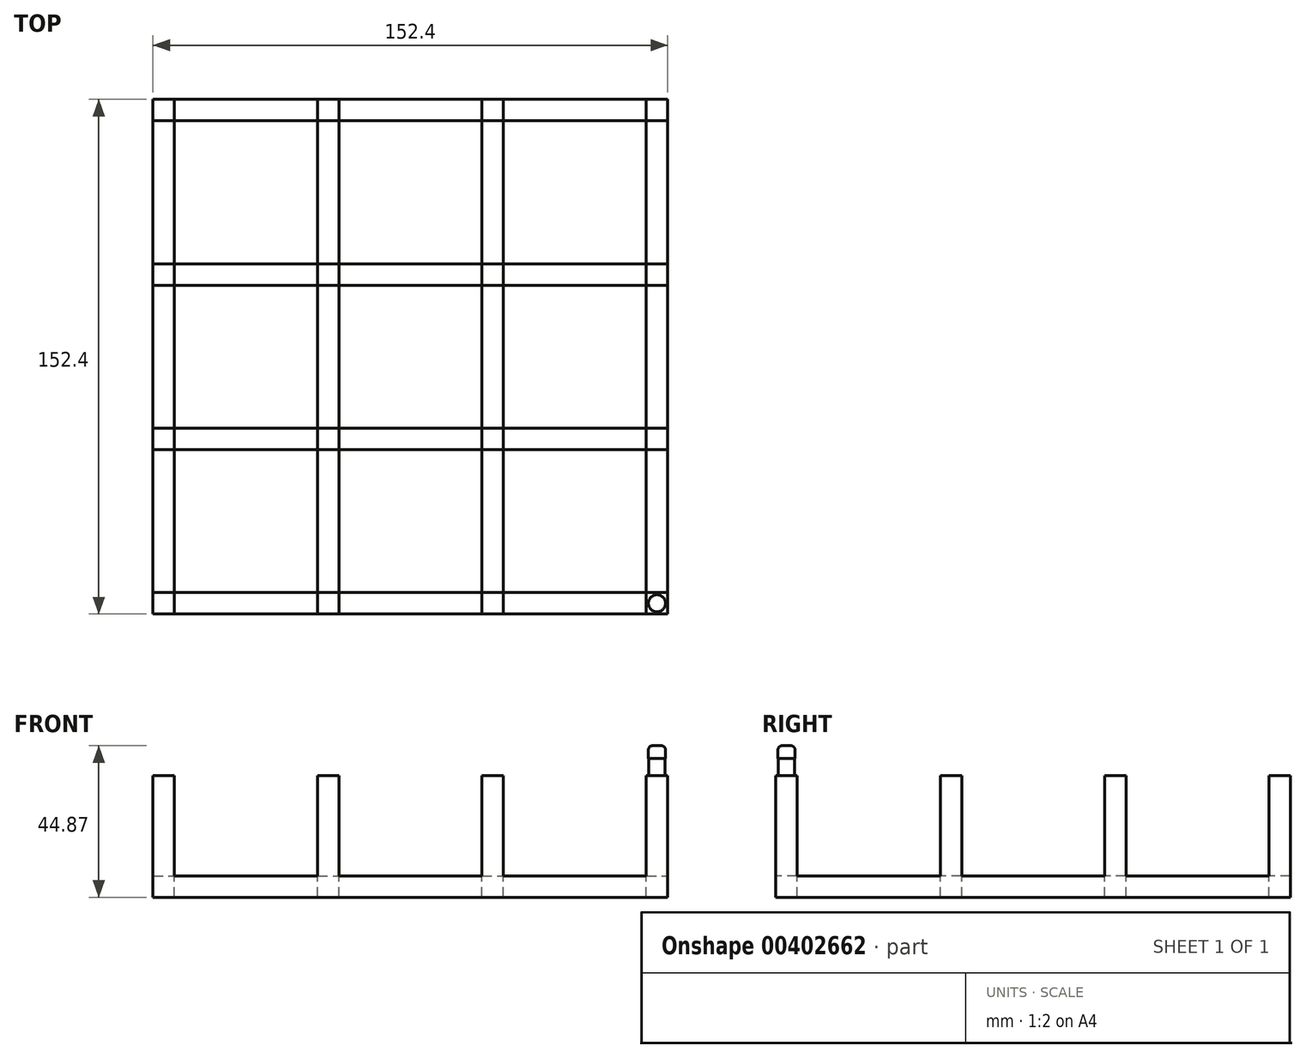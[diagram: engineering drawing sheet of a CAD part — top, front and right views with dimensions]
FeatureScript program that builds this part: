
annotation { "Feature Type Name" : "Feature", "Feature Type Description" : "" }
export const myFeature = defineFeature(function(context is Context, id is Id, definition is map)
    precondition{}
    {
        {
            var Q0;
            Q0=qCreatedBy(makeId("Top.planeOp"),FACE);
            var sketch = newSketch(context, id + "F0", { "sketchPlane" : qUnion([Q0])});
            skLineSegment(sketch, "E0.bottom", {"start": v(0, 0) * mm, "end": v(152.4, 0) * mm});
            skLineSegment(sketch, "E0.top", {"start": v(0, 152.4) * mm, "end": v(152.4, 152.4) * mm});
            skLineSegment(sketch, "E0.left", {"start": v(0, 0) * mm, "end": v(0, 152.4) * mm});
            skLineSegment(sketch, "E0.right", {"start": v(152.4, 0) * mm, "end": v(152.4, 152.4) * mm});
            skSolve(sketch);
        }
        {
            var Q0;
            Q0 = qSketchRegion(id + "F0", true);
            extrude(context, id + "F1", {"entities" : qUnion([Q0]), "depth" : 35.98 * mm});
        }
        {
            var Q0;
            Q0=makeQuery(id+"F1.opExtrude","SWEPT_FACE",FACE,{"disambiguationData":[OSD([sQuery(id+"F0.wireOp",EDGE,"E0.bottom")])]});
            var sketch = newSketch(context, id + "F2", { "sketchPlane" : qUnion([Q0])});
            skLineSegment(sketch, "E1.bottom", {"start": v(6.35, 35.98) * mm, "end": v(48.68, 35.98) * mm});
            skLineSegment(sketch, "E1.top", {"start": v(6.35, 6.35) * mm, "end": v(48.68, 6.35) * mm});
            skLineSegment(sketch, "E1.left", {"start": v(6.35, 35.98) * mm, "end": v(6.35, 6.35) * mm});
            skLineSegment(sketch, "E1.right", {"start": v(48.68, 35.98) * mm, "end": v(48.68, 6.35) * mm});
            skLineSegment(sketch, "E2.bottom", {"start": v(55.03, 35.98) * mm, "end": v(97.37, 35.98) * mm});
            skLineSegment(sketch, "E2.top", {"start": v(55.03, 6.35) * mm, "end": v(97.37, 6.35) * mm});
            skLineSegment(sketch, "E2.left", {"start": v(55.03, 35.98) * mm, "end": v(55.03, 6.35) * mm});
            skLineSegment(sketch, "E2.right", {"start": v(97.37, 35.98) * mm, "end": v(97.37, 6.35) * mm});
            skLineSegment(sketch, "E3.bottom", {"start": v(103.72, 35.98) * mm, "end": v(146.05, 35.98) * mm});
            skLineSegment(sketch, "E3.top", {"start": v(103.72, 6.35) * mm, "end": v(146.05, 6.35) * mm});
            skLineSegment(sketch, "E3.left", {"start": v(103.72, 35.98) * mm, "end": v(103.72, 6.35) * mm});
            skLineSegment(sketch, "E3.right", {"start": v(146.05, 35.98) * mm, "end": v(146.05, 6.35) * mm});
            skSolve(sketch);
        }
        {
            var Q0;
            Q0 = qSketchRegion(id + "F2", true);
            extrude(context, id + "F3", {"entities" : qUnion([Q0]), "operationType" : NewBodyOperationType.REMOVE, "oppositeDirection" : true, "depth" : 396.24 * mm});
        }
        {
            var Q0;
            Q0=makeQuery(id+"F1.opExtrude","SWEPT_FACE",FACE,{"disambiguationData":[OSD([sQuery(id+"F0.wireOp",EDGE,"E0.right")])]});
            var sketch = newSketch(context, id + "F4", { "sketchPlane" : qUnion([Q0])});
            skLineSegment(sketch, "E4.bottom", {"start": v(6.35, 35.98) * mm, "end": v(48.68, 35.98) * mm});
            skLineSegment(sketch, "E4.top", {"start": v(6.35, 6.35) * mm, "end": v(48.68, 6.35) * mm});
            skLineSegment(sketch, "E4.left", {"start": v(6.35, 35.98) * mm, "end": v(6.35, 6.35) * mm});
            skLineSegment(sketch, "E4.right", {"start": v(48.68, 35.98) * mm, "end": v(48.68, 6.35) * mm});
            skLineSegment(sketch, "E5.bottom", {"start": v(55.03, 35.98) * mm, "end": v(97.37, 35.98) * mm});
            skLineSegment(sketch, "E5.top", {"start": v(55.03, 6.35) * mm, "end": v(97.37, 6.35) * mm});
            skLineSegment(sketch, "E5.left", {"start": v(55.03, 35.98) * mm, "end": v(55.03, 6.35) * mm});
            skLineSegment(sketch, "E5.right", {"start": v(97.37, 35.98) * mm, "end": v(97.37, 6.35) * mm});
            skLineSegment(sketch, "E6.bottom", {"start": v(103.72, 35.98) * mm, "end": v(146.05, 35.98) * mm});
            skLineSegment(sketch, "E6.top", {"start": v(103.72, 6.35) * mm, "end": v(146.05, 6.35) * mm});
            skLineSegment(sketch, "E6.left", {"start": v(103.72, 35.98) * mm, "end": v(103.72, 6.35) * mm});
            skLineSegment(sketch, "E6.right", {"start": v(146.05, 35.98) * mm, "end": v(146.05, 6.35) * mm});
            skSolve(sketch);
        }
        {
            var Q0;
            Q0 = qSketchRegion(id + "F4", true);
            extrude(context, id + "F5", {"entities" : qUnion([Q0]), "operationType" : NewBodyOperationType.REMOVE, "oppositeDirection" : true, "depth" : 206.25 * mm});
        }
        {
            var Q0;
            Q0=makeQuery(id+"F5.boolean.opBoolean","MERGE",FACE,{"derivedFrom":[makeQuery(id+"F3.boolean.opBoolean","COPY",FACE,{"derivedFrom":makeQuery(id+"F3.opExtrude","SWEPT_FACE",FACE,{"disambiguationData":[OSD([sQuery(id+"F2.wireOp",EDGE,"E1.top")])]})}),makeQuery(id+"F3.boolean.opBoolean","COPY",FACE,{"derivedFrom":makeQuery(id+"F3.opExtrude","SWEPT_FACE",FACE,{"disambiguationData":[OSD([sQuery(id+"F2.wireOp",EDGE,"E2.top")])]})}),makeQuery(id+"F3.boolean.opBoolean","COPY",FACE,{"derivedFrom":makeQuery(id+"F3.opExtrude","SWEPT_FACE",FACE,{"disambiguationData":[OSD([sQuery(id+"F2.wireOp",EDGE,"E3.top")])]})}),makeQuery(id+"F5.opExtrude","SWEPT_FACE",FACE,{"disambiguationData":[OSD([sQuery(id+"F4.wireOp",EDGE,"E4.top")])]}),makeQuery(id+"F5.opExtrude","SWEPT_FACE",FACE,{"disambiguationData":[OSD([sQuery(id+"F4.wireOp",EDGE,"E5.top")])]}),makeQuery(id+"F5.opExtrude","SWEPT_FACE",FACE,{"disambiguationData":[OSD([sQuery(id+"F4.wireOp",EDGE,"E6.top")])]})]});
            var sketch = newSketch(context, id + "F6", { "sketchPlane" : qUnion([Q0])});
            skLineSegment(sketch, "E7.bottom", {"start": v(6.35, 146.05) * mm, "end": v(48.68, 146.05) * mm});
            skLineSegment(sketch, "E7.top", {"start": v(6.35, 103.72) * mm, "end": v(48.68, 103.72) * mm});
            skLineSegment(sketch, "E7.left", {"start": v(6.35, 146.05) * mm, "end": v(6.35, 103.72) * mm});
            skLineSegment(sketch, "E7.right", {"start": v(48.68, 146.05) * mm, "end": v(48.68, 103.72) * mm});
            skLineSegment(sketch, "E8.bottom", {"start": v(55.03, 146.05) * mm, "end": v(97.37, 146.05) * mm});
            skLineSegment(sketch, "E8.top", {"start": v(55.03, 103.72) * mm, "end": v(97.37, 103.72) * mm});
            skLineSegment(sketch, "E8.left", {"start": v(55.03, 146.05) * mm, "end": v(55.03, 103.72) * mm});
            skLineSegment(sketch, "E8.right", {"start": v(97.37, 146.05) * mm, "end": v(97.37, 103.72) * mm});
            skLineSegment(sketch, "E9.bottom", {"start": v(103.72, 146.05) * mm, "end": v(146.05, 146.05) * mm});
            skLineSegment(sketch, "E9.top", {"start": v(103.72, 103.72) * mm, "end": v(146.05, 103.72) * mm});
            skLineSegment(sketch, "E9.left", {"start": v(103.72, 146.05) * mm, "end": v(103.72, 103.72) * mm});
            skLineSegment(sketch, "E9.right", {"start": v(146.05, 146.05) * mm, "end": v(146.05, 103.72) * mm});
            skLineSegment(sketch, "E10.bottom", {"start": v(6.35, 97.37) * mm, "end": v(48.68, 97.37) * mm});
            skLineSegment(sketch, "E10.top", {"start": v(6.35, 55.03) * mm, "end": v(48.68, 55.03) * mm});
            skLineSegment(sketch, "E10.left", {"start": v(6.35, 97.37) * mm, "end": v(6.35, 55.03) * mm});
            skLineSegment(sketch, "E10.right", {"start": v(48.68, 97.37) * mm, "end": v(48.68, 55.03) * mm});
            skLineSegment(sketch, "E11.bottom", {"start": v(97.37, 97.37) * mm, "end": v(55.03, 97.37) * mm});
            skLineSegment(sketch, "E11.top", {"start": v(97.37, 55.03) * mm, "end": v(55.03, 55.03) * mm});
            skLineSegment(sketch, "E11.left", {"start": v(97.37, 97.37) * mm, "end": v(97.37, 55.03) * mm});
            skLineSegment(sketch, "E11.right", {"start": v(55.03, 97.37) * mm, "end": v(55.03, 55.03) * mm});
            skLineSegment(sketch, "E12.bottom", {"start": v(103.72, 97.37) * mm, "end": v(146.05, 97.37) * mm});
            skLineSegment(sketch, "E12.top", {"start": v(103.72, 55.03) * mm, "end": v(146.05, 55.03) * mm});
            skLineSegment(sketch, "E12.left", {"start": v(103.72, 97.37) * mm, "end": v(103.72, 55.03) * mm});
            skLineSegment(sketch, "E12.right", {"start": v(146.05, 97.37) * mm, "end": v(146.05, 55.03) * mm});
            skLineSegment(sketch, "E13.bottom", {"start": v(6.35, 48.68) * mm, "end": v(48.68, 48.68) * mm});
            skLineSegment(sketch, "E13.top", {"start": v(6.35, 6.35) * mm, "end": v(48.68, 6.35) * mm});
            skLineSegment(sketch, "E13.left", {"start": v(6.35, 48.68) * mm, "end": v(6.35, 6.35) * mm});
            skLineSegment(sketch, "E13.right", {"start": v(48.68, 48.68) * mm, "end": v(48.68, 6.35) * mm});
            skLineSegment(sketch, "E14.bottom", {"start": v(55.03, 48.68) * mm, "end": v(97.37, 48.68) * mm});
            skLineSegment(sketch, "E14.top", {"start": v(55.03, 6.35) * mm, "end": v(97.37, 6.35) * mm});
            skLineSegment(sketch, "E14.left", {"start": v(55.03, 48.68) * mm, "end": v(55.03, 6.35) * mm});
            skLineSegment(sketch, "E14.right", {"start": v(97.37, 48.68) * mm, "end": v(97.37, 6.35) * mm});
            skLineSegment(sketch, "E15.bottom", {"start": v(103.72, 48.68) * mm, "end": v(146.05, 48.68) * mm});
            skLineSegment(sketch, "E15.top", {"start": v(103.72, 6.35) * mm, "end": v(146.05, 6.35) * mm});
            skLineSegment(sketch, "E15.left", {"start": v(103.72, 48.68) * mm, "end": v(103.72, 6.35) * mm});
            skLineSegment(sketch, "E15.right", {"start": v(146.05, 48.68) * mm, "end": v(146.05, 6.35) * mm});
            skSolve(sketch);
        }
        {
            var Q0;
            Q0 = qSketchRegion(id + "F6", true);
            extrude(context, id + "F7", {"entities" : qUnion([Q0]), "operationType" : NewBodyOperationType.REMOVE, "oppositeDirection" : true, "depth" : 25.4 * mm});
        }
        {
            var Q0;
            {var subQ0=sQuery(id+"F0.wireOp",EDGE,"E0.bottom");var subQ1=makeQuery(id+"F1.opExtrude","SWEPT_FACE",FACE,{"disambiguationData":[OSD([subQ0])]});var subQ2=sQuery(id+"F0.wireOp",EDGE,"E0.right");var subQ3=makeQuery(id+"F1.opExtrude","SWEPT_FACE",FACE,{"disambiguationData":[OSD([subQ2])]});var subQ5=sQuery(id+"F0.wireOp",EDGE,"E0.top");Q0=makeQuery(id+"F5.boolean.opBoolean","SPLIT",FACE,{"disambiguationData":[TD([subQ1])],"derivedFrom":makeQuery(id+"F3.boolean.opBoolean","SPLIT",FACE,{"disambiguationData":[TD([subQ3])],"derivedFrom":makeQuery(id+"F1.opExtrude","CAP_FACE",FACE,{"disambiguationData":[OSD([subQ0,subQ5,sQuery(id+"F0.wireOp",EDGE,"E0.left"),subQ2])],"isStart":false})})});}
            var sketch = newSketch(context, id + "F8", { "sketchPlane" : qUnion([Q0])});
            skCircle(sketch, "E16", {"center": v(149.22, 3.18) * mm, "radius": 2.41 * mm});
            skPoint(sketch, "E16.centerSnap0", {"position": v(152.4, 3.17) * mm});
            skSolve(sketch);
        }
        {
            var Q0;
            Q0 = qSketchRegion(id + "F8", true);
            extrude(context, id + "F9", {"entities" : qUnion([Q0]), "operationType" : NewBodyOperationType.ADD, "depth" : 5.08 * mm});
        }
        {
            var Q0;
            Q0=makeQuery(id+"F9.opExtrude","CAP_FACE",FACE,{"disambiguationData":[OSD([sQuery(id+"F8.wireOp",EDGE,"E16")])],"isStart":false});
            var sketch = newSketch(context, id + "F10", { "sketchPlane" : qUnion([Q0])});
            skCircle(sketch, "E17", {"center": v(149.22, 3.18) * mm, "radius": 2.54 * mm});
            skSolve(sketch);
        }
        {
            var Q0;
            Q0 = qSketchRegion(id + "F10", true);
            extrude(context, id + "F11", {"entities" : qUnion([Q0]), "operationType" : NewBodyOperationType.ADD, "depth" : 3.8 * mm});
        }
        {
            var Q0;
            Q0=makeQuery(id+"F11.opExtrude","CAP_EDGE",EDGE,{"disambiguationData":[OSD([sQuery(id+"F10.wireOp",EDGE,"E17")])],"isStart":false});
            fillet(context, id + "F12", {"entities" : qUnion([Q0]), "radius" : 1.27 * mm, "tangentPropagation" : true, "allowEdgeOverflow" : false});
        }
    });
